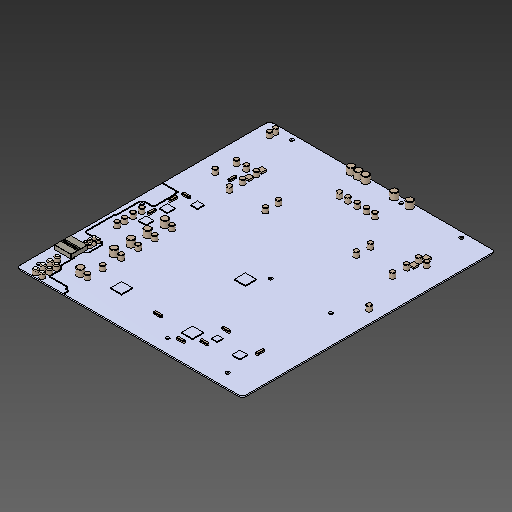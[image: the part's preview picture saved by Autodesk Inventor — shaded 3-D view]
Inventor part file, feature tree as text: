
AUTODESK INVENTOR PART (.ipt)
format: ipt  version: 2018.2 (Build 222227000, 227)  size: 489,984 bytes
history: native  units: mm
features: other x3, fillet x1
ambient origin geometry x8: Origin, YZ Plane, XZ Plane, XY Plane, X Axis, Y Axis, Z Axis, Center Point
bodies: Body1 (feature_tree), Body2 (feature_tree)
feature tree (4):
  other  "ソリッド1"
  other  "ソリッド2"
  other  "Cut-Extrude2"
  fillet  "Fillet6"  [1 undecoded]
note: 1 required parameter value undecoded (feature->parameter linkage not recoverable at this tier; creation-order binding heuristic only, values carry confidence <= 0.55)
